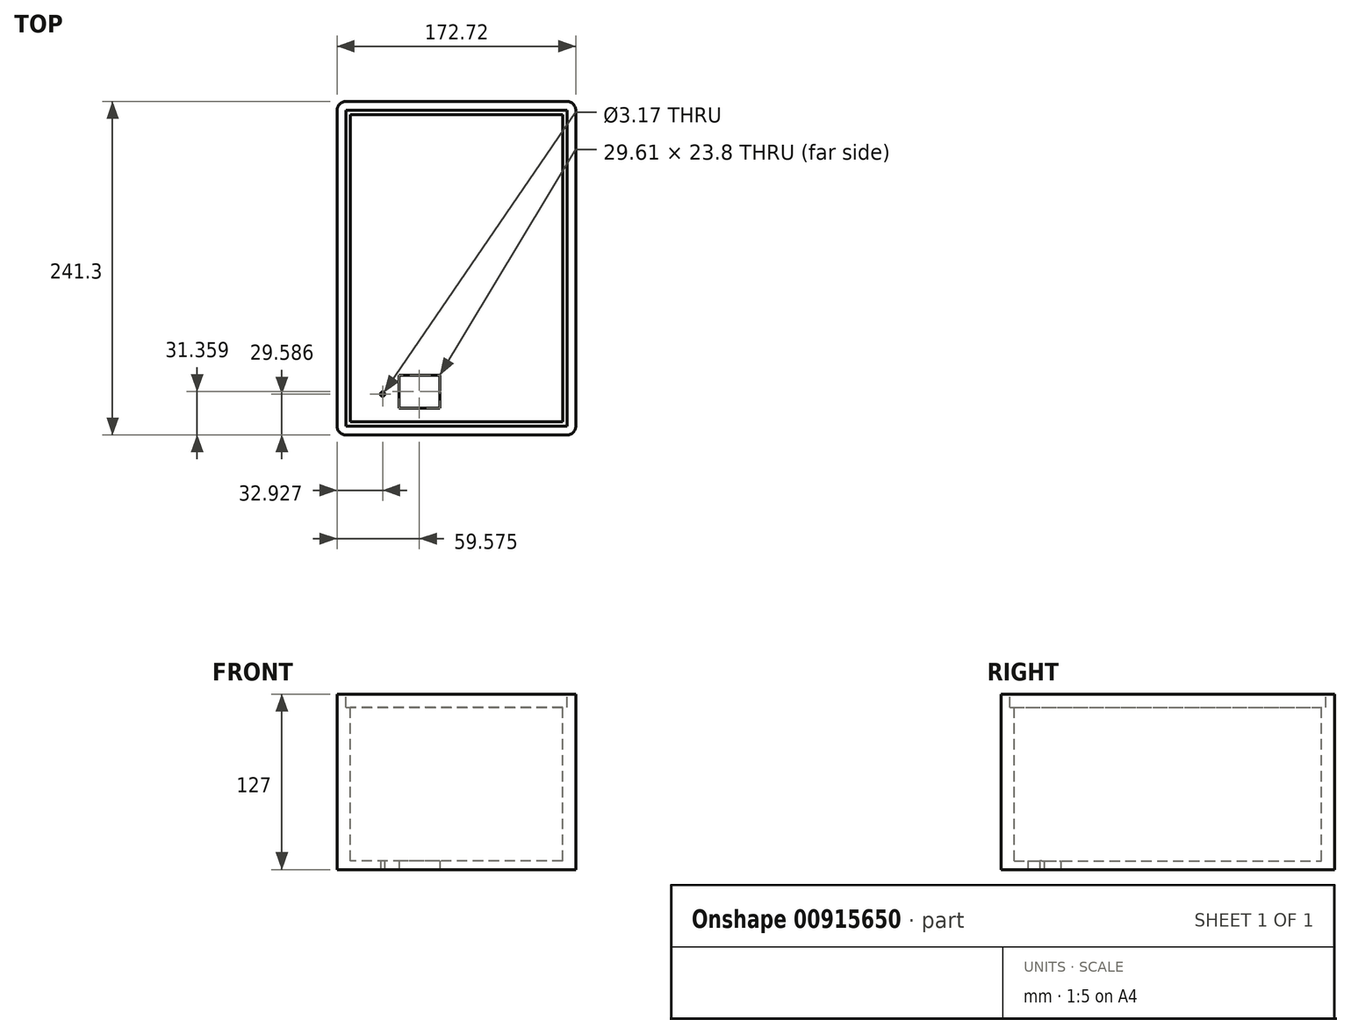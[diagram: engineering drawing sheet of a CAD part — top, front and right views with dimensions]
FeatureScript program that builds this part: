
annotation { "Feature Type Name" : "Feature", "Feature Type Description" : "" }
export const myFeature = defineFeature(function(context is Context, id is Id, definition is map)
    precondition{}
    {
        {
            var Q0;
            Q0=qCreatedBy(makeId("Top.planeOp"),FACE);
            var sketch = newSketch(context, id + "F0", { "sketchPlane" : qUnion([Q0])});
            skLineSegment(sketch, "E0.bottom", {"start": v(-27.54, 0) * mm, "end": v(132.48, 0) * mm});
            skLineSegment(sketch, "E0.top", {"start": v(-27.54, 241.3) * mm, "end": v(132.48, 241.3) * mm});
            skLineSegment(sketch, "E0.left", {"start": v(-33.9, 6.35) * mm, "end": v(-33.9, 234.95) * mm});
            skLineSegment(sketch, "E0.right", {"start": v(138.83, 6.35) * mm, "end": v(138.83, 234.95) * mm});
            skPoint(sketch, "E1.visualSharp", {"position": v(-33.9, 0) * mm});
            skArc(sketch, "E1.filletArc", {"start": v(-33.9, 6.35) * mm, "mid": v(-32.03, 1.86) * mm, "end": v(-27.54, 0) * mm});
            skPoint(sketch, "E2.visualSharp", {"position": v(138.83, 0) * mm});
            skArc(sketch, "E2.filletArc", {"start": v(132.48, 0) * mm, "mid": v(136.97, 1.86) * mm, "end": v(138.83, 6.35) * mm});
            skPoint(sketch, "E3.visualSharp", {"position": v(138.83, 241.3) * mm});
            skArc(sketch, "E3.filletArc", {"start": v(138.83, 234.95) * mm, "mid": v(136.97, 239.44) * mm, "end": v(132.48, 241.3) * mm});
            skPoint(sketch, "E4.visualSharp", {"position": v(-33.9, 241.3) * mm});
            skArc(sketch, "E4.filletArc", {"start": v(-27.54, 241.3) * mm, "mid": v(-32.03, 239.44) * mm, "end": v(-33.9, 234.95) * mm});
            skSolve(sketch);
        }
        {
            var Q0;
            Q0=makeQuery(id+"F0.imprint","IMPRINT",FACE,{"disambiguationData":[TD([[makeQuery(id+"F0.imprint","IMPRINT",EDGE,{"derivedFrom":sQuery(id+"F0.wireOp",EDGE,"E0.bottom")}),1.0]])]});
            extrude(context, id + "F1", {"entities" : qUnion([Q0]), "depth" : 127 * mm, "offsetDistance" : 25.4 * mm});
        }
        {
            var Q0;
            Q0=makeQuery(id+"F1.opExtrude","CAP_FACE",FACE,{"disambiguationData":[OSD([sQuery(id+"F0.wireOp",EDGE,"E0.bottom"),sQuery(id+"F0.wireOp",EDGE,"E0.top"),sQuery(id+"F0.wireOp",EDGE,"E0.left"),sQuery(id+"F0.wireOp",EDGE,"E0.right"),sQuery(id+"F0.wireOp",EDGE,"E1.filletArc"),sQuery(id+"F0.wireOp",EDGE,"E2.filletArc"),sQuery(id+"F0.wireOp",EDGE,"E3.filletArc"),sQuery(id+"F0.wireOp",EDGE,"E4.filletArc")])],"isStart":false});
            shell(context, id + "F2", {"entities" : qUnion([Q0]), "thickness" : 6.35 * mm});
        }
        {
            var Q0;
            Q0=makeQuery(id+"F1.opExtrude","CAP_FACE",FACE,{"disambiguationData":[OSD([sQuery(id+"F0.wireOp",EDGE,"E0.bottom"),sQuery(id+"F0.wireOp",EDGE,"E0.top"),sQuery(id+"F0.wireOp",EDGE,"E0.left"),sQuery(id+"F0.wireOp",EDGE,"E0.right"),sQuery(id+"F0.wireOp",EDGE,"E1.filletArc"),sQuery(id+"F0.wireOp",EDGE,"E2.filletArc"),sQuery(id+"F0.wireOp",EDGE,"E3.filletArc"),sQuery(id+"F0.wireOp",EDGE,"E4.filletArc")])],"isStart":false});
            var sketch = newSketch(context, id + "F3", { "sketchPlane" : qUnion([Q0])});
            skLineSegment(sketch, "E5.0", {"start": v(129.3, 231.78) * mm, "end": v(-24.37, 231.78) * mm});
            skLineSegment(sketch, "E5.1", {"start": v(129.3, 9.53) * mm, "end": v(129.3, 231.78) * mm});
            skLineSegment(sketch, "E5.2", {"start": v(-24.37, 9.53) * mm, "end": v(129.3, 9.53) * mm});
            skLineSegment(sketch, "E5.3", {"start": v(-24.37, 231.78) * mm, "end": v(-24.37, 9.53) * mm});
            skLineSegment(sketch, "E6.0", {"start": v(132.48, 234.95) * mm, "end": v(-27.54, 234.95) * mm});
            skLineSegment(sketch, "E6.1", {"start": v(132.48, 6.35) * mm, "end": v(132.48, 234.95) * mm});
            skLineSegment(sketch, "E6.2", {"start": v(-27.54, 6.35) * mm, "end": v(132.48, 6.35) * mm});
            skLineSegment(sketch, "E6.3", {"start": v(-27.54, 234.95) * mm, "end": v(-27.54, 6.35) * mm});
            skSolve(sketch);
        }
        {
            var Q0;
            Q0 = qSketchRegion(id + "F3", true);
            extrude(context, id + "F4", {"entities" : qUnion([Q0]), "operationType" : NewBodyOperationType.ADD, "oppositeDirection" : true, "depth" : 127 * mm, "offsetDistance" : 25.4 * mm});
        }
        {
            var Q0;
            Q0 = qSketchRegion(id + "F3", true);
            extrude(context, id + "F5", {"entities" : qUnion([Q0]), "operationType" : NewBodyOperationType.REMOVE, "oppositeDirection" : true, "depth" : 9.52 * mm, "offsetDistance" : 25.4 * mm});
        }
        {
            var Q0;
            Q0=makeQuery(id+"F1.opExtrude","CAP_FACE",FACE,{"disambiguationData":[OSD([sQuery(id+"F0.wireOp",EDGE,"E0.bottom"),sQuery(id+"F0.wireOp",EDGE,"E0.top"),sQuery(id+"F0.wireOp",EDGE,"E0.left"),sQuery(id+"F0.wireOp",EDGE,"E0.right"),sQuery(id+"F0.wireOp",EDGE,"E1.filletArc"),sQuery(id+"F0.wireOp",EDGE,"E2.filletArc"),sQuery(id+"F0.wireOp",EDGE,"E3.filletArc"),sQuery(id+"F0.wireOp",EDGE,"E4.filletArc")])],"isStart":true});
            var sketch = newSketch(context, id + "F6", { "sketchPlane" : qUnion([Q0])});
            skCircle(sketch, "E7", {"center": v(-0.96, -29.59) * mm, "radius": 1.59 * mm});
            skSolve(sketch);
        }
        {
            var Q0;
            Q0=makeQuery(id+"F6.imprint","IMPRINT",FACE,{"disambiguationData":[TD([[makeQuery(id+"F6.imprint","IMPRINT",EDGE,{"derivedFrom":sQuery(id+"F6.wireOp",EDGE,"E7")}),1.0]])]});
            var Q1;
            Q1=sQuery(id+"F6.wireOp",EDGE,"E7");
            extrude(context, id + "F7", {"entities" : qUnion([Q0]), "operationType" : NewBodyOperationType.REMOVE, "surfaceOperationType" : NewSurfaceOperationType.ADD, "surfaceEntities" : qUnion([Q1]), "oppositeDirection" : true, "depth" : 25.4 * mm, "offsetDistance" : 25.4 * mm});
        }
        {
            var Q0;
            Q0=makeQuery(id+"F1.opExtrude","CAP_FACE",FACE,{"disambiguationData":[OSD([sQuery(id+"F0.wireOp",EDGE,"E0.bottom"),sQuery(id+"F0.wireOp",EDGE,"E0.top"),sQuery(id+"F0.wireOp",EDGE,"E0.left"),sQuery(id+"F0.wireOp",EDGE,"E0.right"),sQuery(id+"F0.wireOp",EDGE,"E1.filletArc"),sQuery(id+"F0.wireOp",EDGE,"E2.filletArc"),sQuery(id+"F0.wireOp",EDGE,"E3.filletArc"),sQuery(id+"F0.wireOp",EDGE,"E4.filletArc")])],"isStart":true});
            var sketch = newSketch(context, id + "F8", { "sketchPlane" : qUnion([Q0])});
            skLineSegment(sketch, "E8.bottom", {"start": v(10.88, -43.26) * mm, "end": v(40.49, -43.26) * mm});
            skLineSegment(sketch, "E8.top", {"start": v(10.88, -19.46) * mm, "end": v(40.49, -19.46) * mm});
            skLineSegment(sketch, "E8.left", {"start": v(10.88, -43.26) * mm, "end": v(10.88, -19.46) * mm});
            skLineSegment(sketch, "E8.right", {"start": v(40.49, -43.26) * mm, "end": v(40.49, -19.46) * mm});
            skSolve(sketch);
        }
        {
            var Q0;
            Q0=makeQuery(id+"F8.imprint","IMPRINT",FACE,{"disambiguationData":[TD([[makeQuery(id+"F8.imprint","IMPRINT",EDGE,{"derivedFrom":sQuery(id+"F8.wireOp",EDGE,"E8.bottom")}),1.0]])]});
            extrude(context, id + "F9", {"entities" : qUnion([Q0]), "operationType" : NewBodyOperationType.REMOVE, "oppositeDirection" : true, "depth" : 25.4 * mm, "offsetDistance" : 25.4 * mm});
        }
    });
